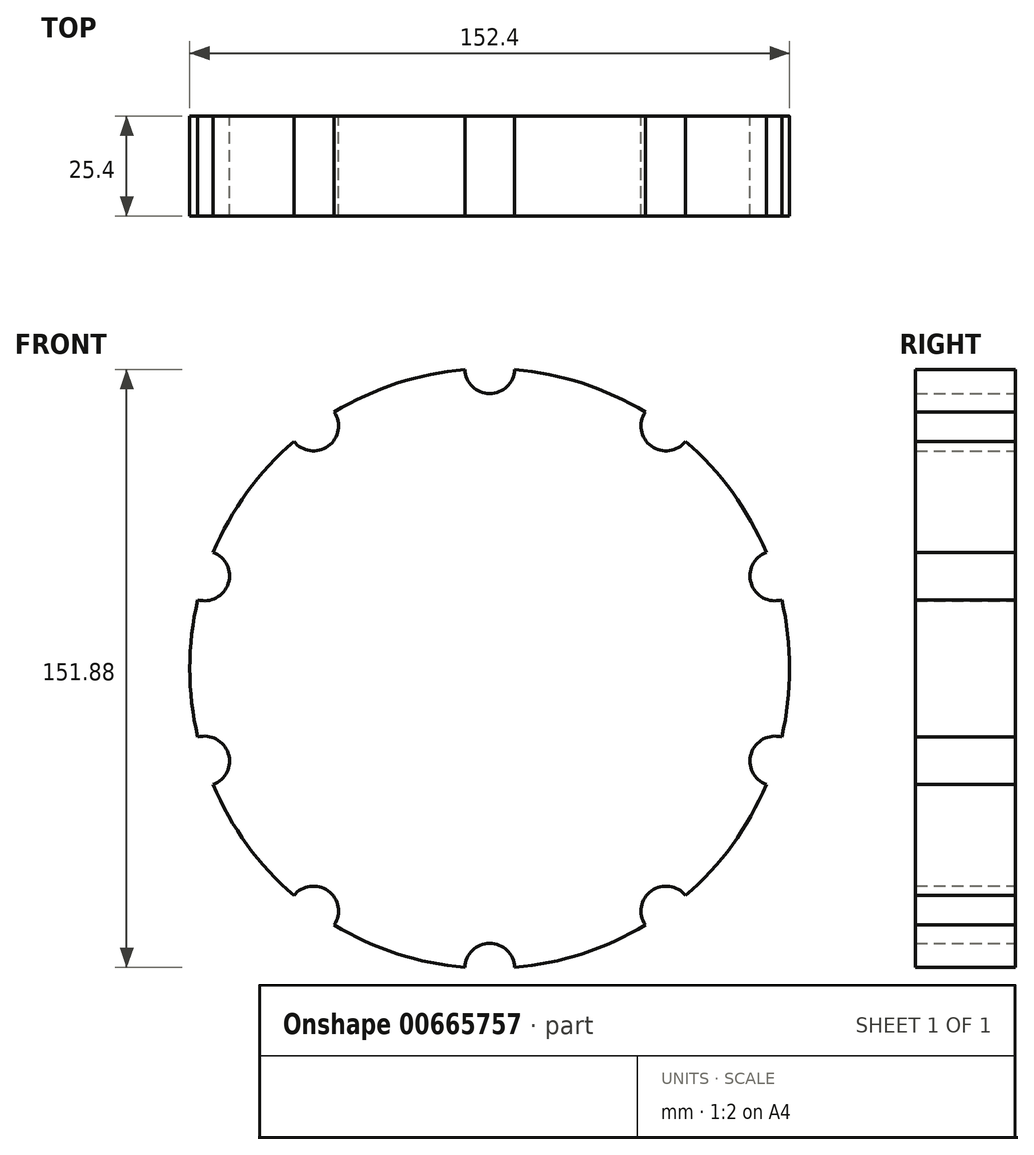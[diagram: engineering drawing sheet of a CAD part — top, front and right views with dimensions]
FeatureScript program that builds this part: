
annotation { "Feature Type Name" : "Feature", "Feature Type Description" : "" }
export const myFeature = defineFeature(function(context is Context, id is Id, definition is map)
    precondition{}
    {
        {
            var Q0;
            Q0=qCreatedBy(makeId("Front.planeOp"),FACE);
            var sketch = newSketch(context, id + "F0", { "sketchPlane" : qUnion([Q0])});
            skCircle(sketch, "E0", {"center": v(0, 0) * mm, "radius": 76.2 * mm});
            skCircle(sketch, "E1", {"center": v(0, 76.2) * mm, "radius": 6.35 * mm});
            skCircle(sketch, "E2.1.1", {"center": v(-44.79, 61.65) * mm, "radius": 6.35 * mm});
            skCircle(sketch, "E2.2.1", {"center": v(-72.47, 23.55) * mm, "radius": 6.35 * mm});
            skCircle(sketch, "E2.3.1", {"center": v(-72.47, -23.55) * mm, "radius": 6.35 * mm});
            skCircle(sketch, "E2.4.1", {"center": v(-44.79, -61.65) * mm, "radius": 6.35 * mm});
            skCircle(sketch, "E2.5.1", {"center": v(0, -76.2) * mm, "radius": 6.35 * mm});
            skCircle(sketch, "E2.6.1", {"center": v(44.79, -61.65) * mm, "radius": 6.35 * mm});
            skCircle(sketch, "E2.7.1", {"center": v(72.47, -23.55) * mm, "radius": 6.35 * mm});
            skCircle(sketch, "E2.8.1", {"center": v(72.47, 23.55) * mm, "radius": 6.35 * mm});
            skCircle(sketch, "E2.9.1", {"center": v(44.79, 61.65) * mm, "radius": 6.35 * mm});
            skSolve(sketch);
        }
        {
            var Q0;
            {var subQ0=sQuery(id+"F0.wireOp",EDGE,"E0");var subQ18=sQuery(id+"F0.wireOp",EDGE,"E1");var subQ19=makeQuery(id+"F0.imprint","INTERSECT",VERTEX,{"disambiguationData":[OD(0.0)],"derivedFrom":[subQ18,subQ0]});Q0=makeQuery(id+"F0.imprint","IMPRINT",FACE,{"disambiguationData":[TD([[makeQuery(id+"F0.imprint","IMPRINT",EDGE,{"disambiguationData":[TD([[subQ19,1.0]])],"derivedFrom":subQ18}),-1.0]])]});}
            extrude(context, id + "F1", {"entities" : qUnion([Q0]), "depth" : 25.4 * mm, "offsetDistance" : 25.4 * mm});
        }
    });
